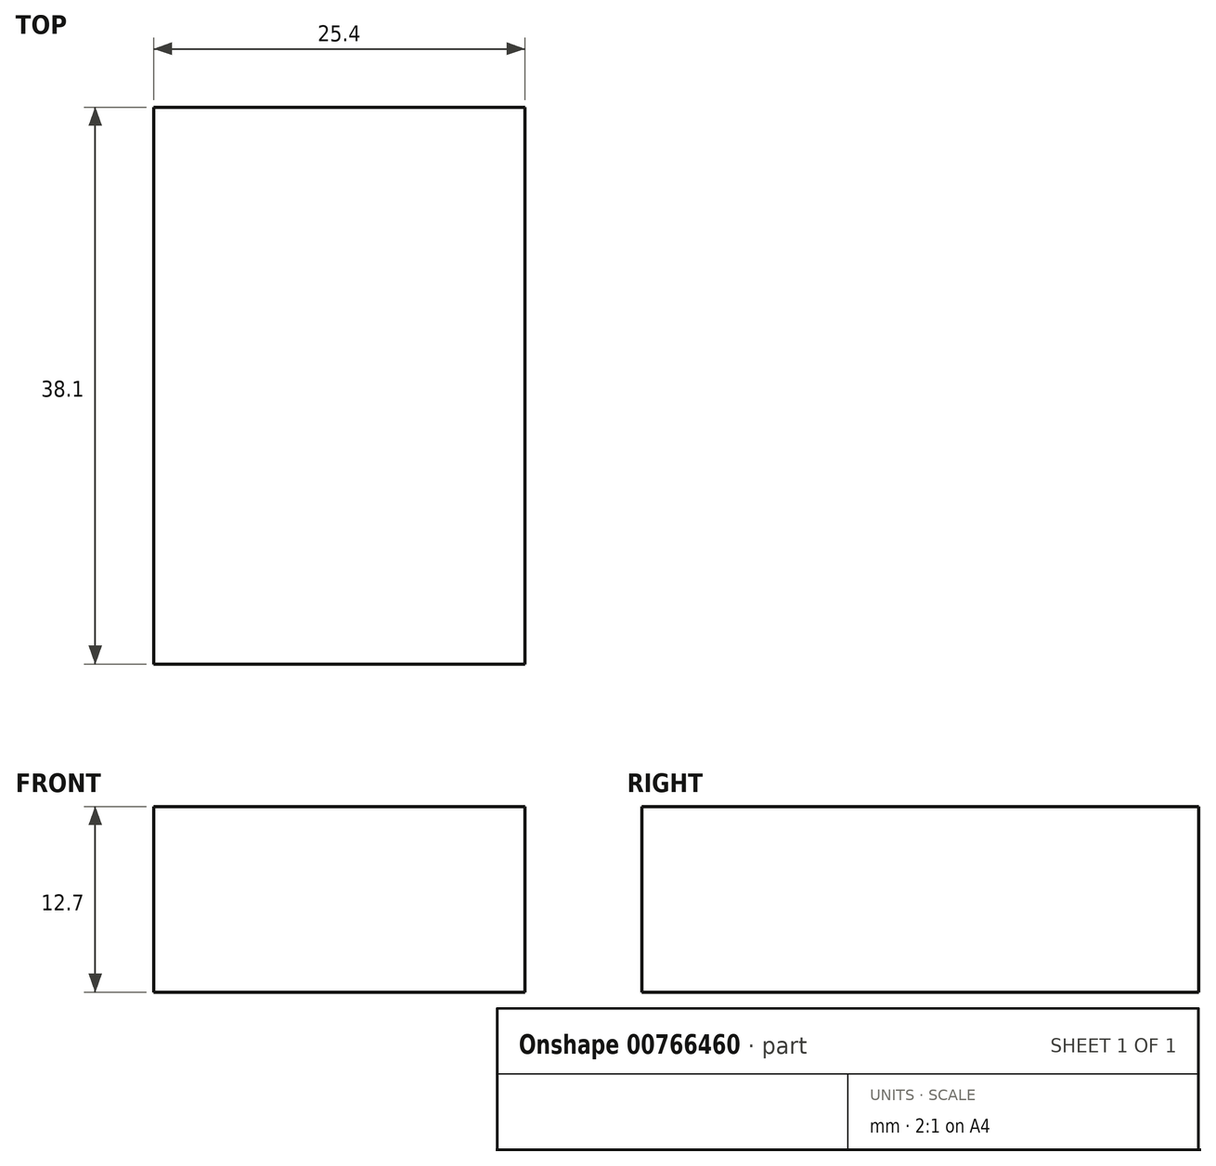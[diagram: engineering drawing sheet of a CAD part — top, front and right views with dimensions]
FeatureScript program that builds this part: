
annotation { "Feature Type Name" : "Feature", "Feature Type Description" : "" }
export const myFeature = defineFeature(function(context is Context, id is Id, definition is map)
    precondition{}
    {
        {
            var Q0;
            Q0=qCreatedBy(makeId("Front.planeOp"),FACE);
            var sketch = newSketch(context, id + "F0", { "sketchPlane" : qUnion([Q0])});
            skLineSegment(sketch, "E0.bottom", {"start": v(-25.4, 0) * mm, "end": v(0, 0) * mm});
            skLineSegment(sketch, "E0.top", {"start": v(-25.4, 12.7) * mm, "end": v(0, 12.7) * mm});
            skLineSegment(sketch, "E0.left", {"start": v(-25.4, 0) * mm, "end": v(-25.4, 12.7) * mm});
            skLineSegment(sketch, "E0.right", {"start": v(0, 0) * mm, "end": v(0, 12.7) * mm});
            skSolve(sketch);
        }
        {
            var Q0;
            Q0=makeQuery(id+"F0.imprint","IMPRINT",FACE,{"disambiguationData":[TD([[makeQuery(id+"F0.imprint","IMPRINT",EDGE,{"derivedFrom":sQuery(id+"F0.wireOp",EDGE,"E0.bottom")}),1.0]])]});
            extrude(context, id + "F1", {"entities" : qUnion([Q0]), "depth" : 38.1 * mm, "offsetDistance" : 25.4 * mm});
        }
    });
